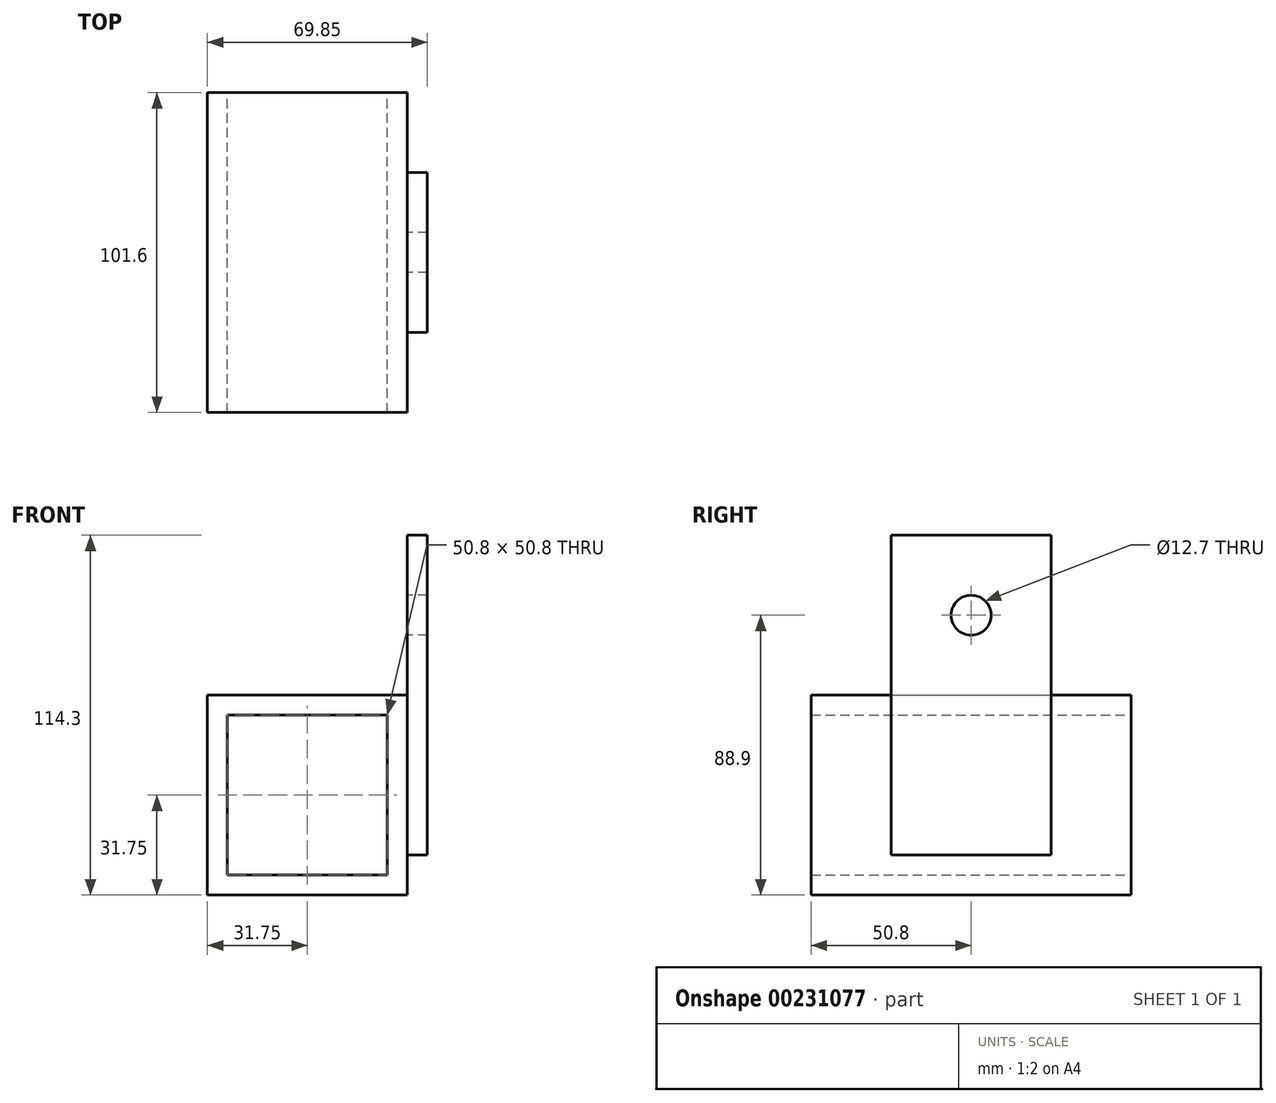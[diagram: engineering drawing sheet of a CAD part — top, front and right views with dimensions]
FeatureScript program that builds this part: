
annotation { "Feature Type Name" : "Feature", "Feature Type Description" : "" }
export const myFeature = defineFeature(function(context is Context, id is Id, definition is map)
    precondition{}
    {
        {
            var Q0;
            Q0=qCreatedBy(makeId("Front.planeOp"),FACE);
            var sketch = newSketch(context, id + "F0", { "sketchPlane" : qUnion([Q0])});
            skLineSegment(sketch, "E0.bottom", {"start": v(0, 0) * mm, "end": v(50.8, 0) * mm});
            skLineSegment(sketch, "E0.top", {"start": v(0, 50.8) * mm, "end": v(50.8, 50.8) * mm});
            skLineSegment(sketch, "E0.left", {"start": v(0, 0) * mm, "end": v(0, 50.8) * mm});
            skLineSegment(sketch, "E0.right", {"start": v(50.8, 0) * mm, "end": v(50.8, 50.8) * mm});
            skLineSegment(sketch, "E1.0", {"start": v(-6.35, -6.35) * mm, "end": v(-6.35, 57.15) * mm});
            skLineSegment(sketch, "E1.1", {"start": v(-6.35, -6.35) * mm, "end": v(57.15, -6.35) * mm});
            skLineSegment(sketch, "E1.2", {"start": v(57.15, -6.35) * mm, "end": v(57.15, 57.15) * mm});
            skLineSegment(sketch, "E1.3", {"start": v(-6.35, 57.15) * mm, "end": v(57.15, 57.15) * mm});
            skSolve(sketch);
        }
        {
            var Q0;
            Q0 = qSketchRegion(id + "F0", true);
            extrude(context, id + "F1", {"entities" : qUnion([Q0]), "depth" : 101.6 * mm});
        }
        {
            var Q0;
            Q0=makeQuery(id+"F1.opExtrude","SWEPT_FACE",FACE,{"disambiguationData":[OSD([sQuery(id+"F0.wireOp",EDGE,"E1.2")])]});
            var sketch = newSketch(context, id + "F2", { "sketchPlane" : qUnion([Q0])});
            skLineSegment(sketch, "E2.bottom", {"start": v(-76.2, 6.35) * mm, "end": v(-25.4, 6.35) * mm});
            skLineSegment(sketch, "E2.top", {"start": v(-76.2, 107.95) * mm, "end": v(-25.4, 107.95) * mm});
            skLineSegment(sketch, "E2.left", {"start": v(-76.2, 6.35) * mm, "end": v(-76.2, 107.95) * mm});
            skLineSegment(sketch, "E2.right", {"start": v(-25.4, 6.35) * mm, "end": v(-25.4, 107.95) * mm});
            skCircle(sketch, "E3", {"center": v(-50.8, 82.55) * mm, "radius": 6.35 * mm});
            skSolve(sketch);
        }
        {
            var Q0;
            Q0 = qSketchRegion(id + "F2", true);
            extrude(context, id + "F3", {"entities" : qUnion([Q0]), "operationType" : NewBodyOperationType.ADD, "depth" : 6.35 * mm});
        }
    });
